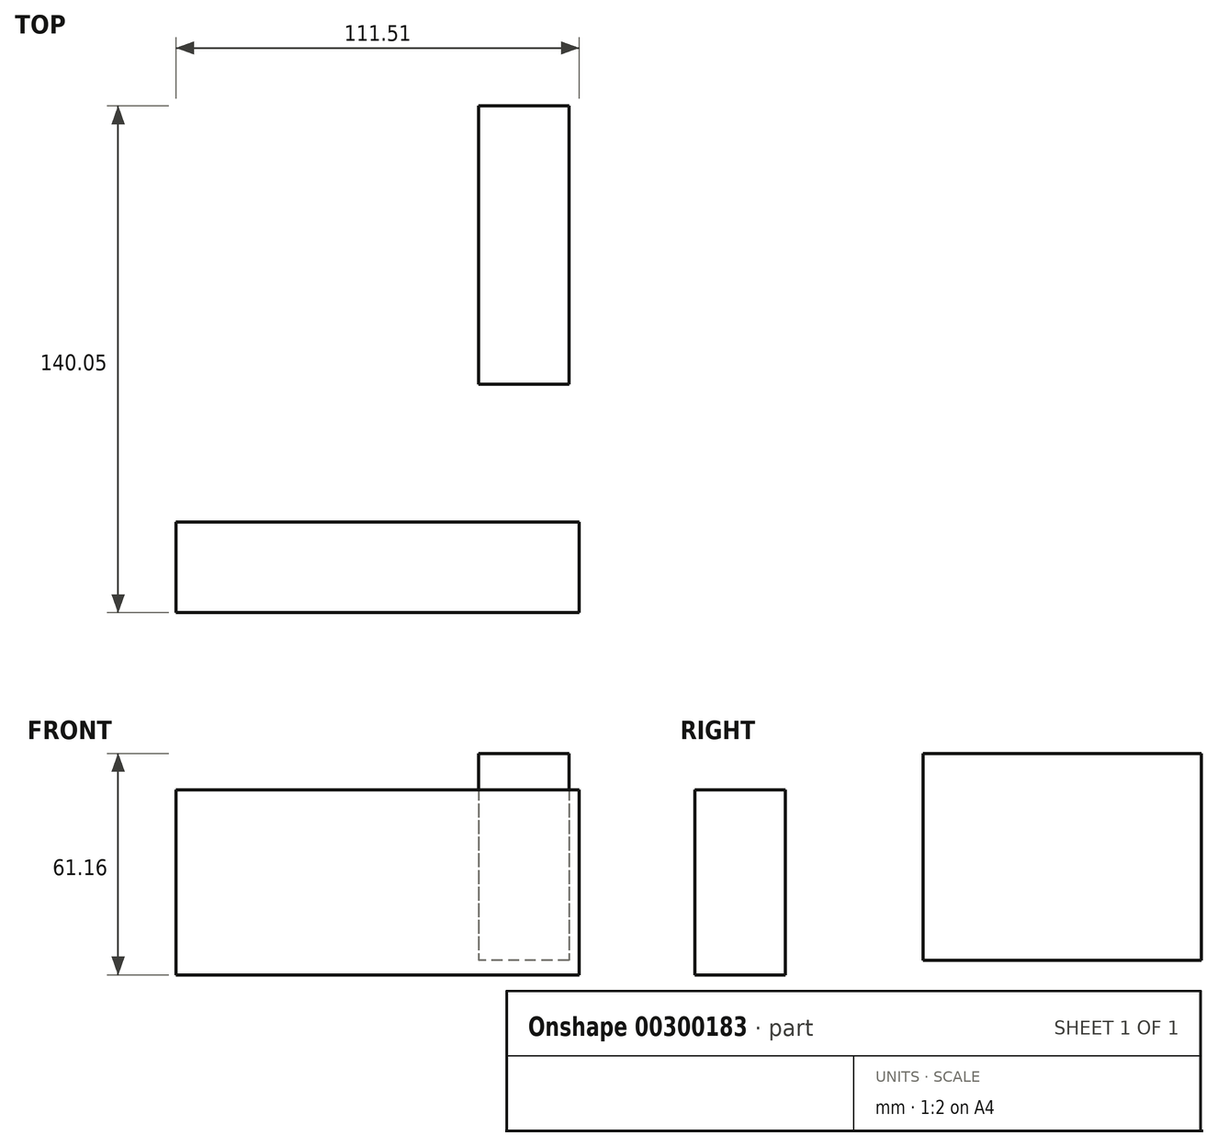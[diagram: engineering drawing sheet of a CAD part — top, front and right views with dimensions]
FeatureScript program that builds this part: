
annotation { "Feature Type Name" : "Feature", "Feature Type Description" : "" }
export const myFeature = defineFeature(function(context is Context, id is Id, definition is map)
    precondition{}
    {
        {
            var Q0;
            Q0=qCreatedBy(makeId("Front.planeOp"),FACE);
            var sketch = newSketch(context, id + "F0", { "sketchPlane" : qUnion([Q0])});
            skLineSegment(sketch, "E0.bottom", {"start": v(-83.69, 51.16) * mm, "end": v(27.82, 51.16) * mm});
            skLineSegment(sketch, "E0.top", {"start": v(-83.69, 0) * mm, "end": v(27.82, 0) * mm});
            skLineSegment(sketch, "E0.left", {"start": v(-83.69, 51.16) * mm, "end": v(-83.69, 0) * mm});
            skLineSegment(sketch, "E0.right", {"start": v(27.82, 51.16) * mm, "end": v(27.82, 0) * mm});
            skSolve(sketch);
        }
        {
            var Q0;
            Q0 = qSketchRegion(id + "F0", true);
            extrude(context, id + "F1", {"entities" : qUnion([Q0]), "depth" : 25 * mm});
        }
        {
            var Q0;
            Q0=qCreatedBy(makeId("Right.planeOp"),FACE);
            var sketch = newSketch(context, id + "F2", { "sketchPlane" : qUnion([Q0])});
            skLineSegment(sketch, "E1.bottom", {"start": v(38.1, 61.16) * mm, "end": v(115.05, 61.16) * mm});
            skLineSegment(sketch, "E1.top", {"start": v(38.1, 4) * mm, "end": v(115.05, 4) * mm});
            skLineSegment(sketch, "E1.left", {"start": v(38.1, 61.16) * mm, "end": v(38.1, 4) * mm});
            skLineSegment(sketch, "E1.right", {"start": v(115.05, 61.16) * mm, "end": v(115.05, 4) * mm});
            skSolve(sketch);
        }
        {
            var Q0;
            Q0 = qSketchRegion(id + "F2", true);
            extrude(context, id + "F3", {"entities" : qUnion([Q0]), "depth" : 25 * mm});
        }
    });
